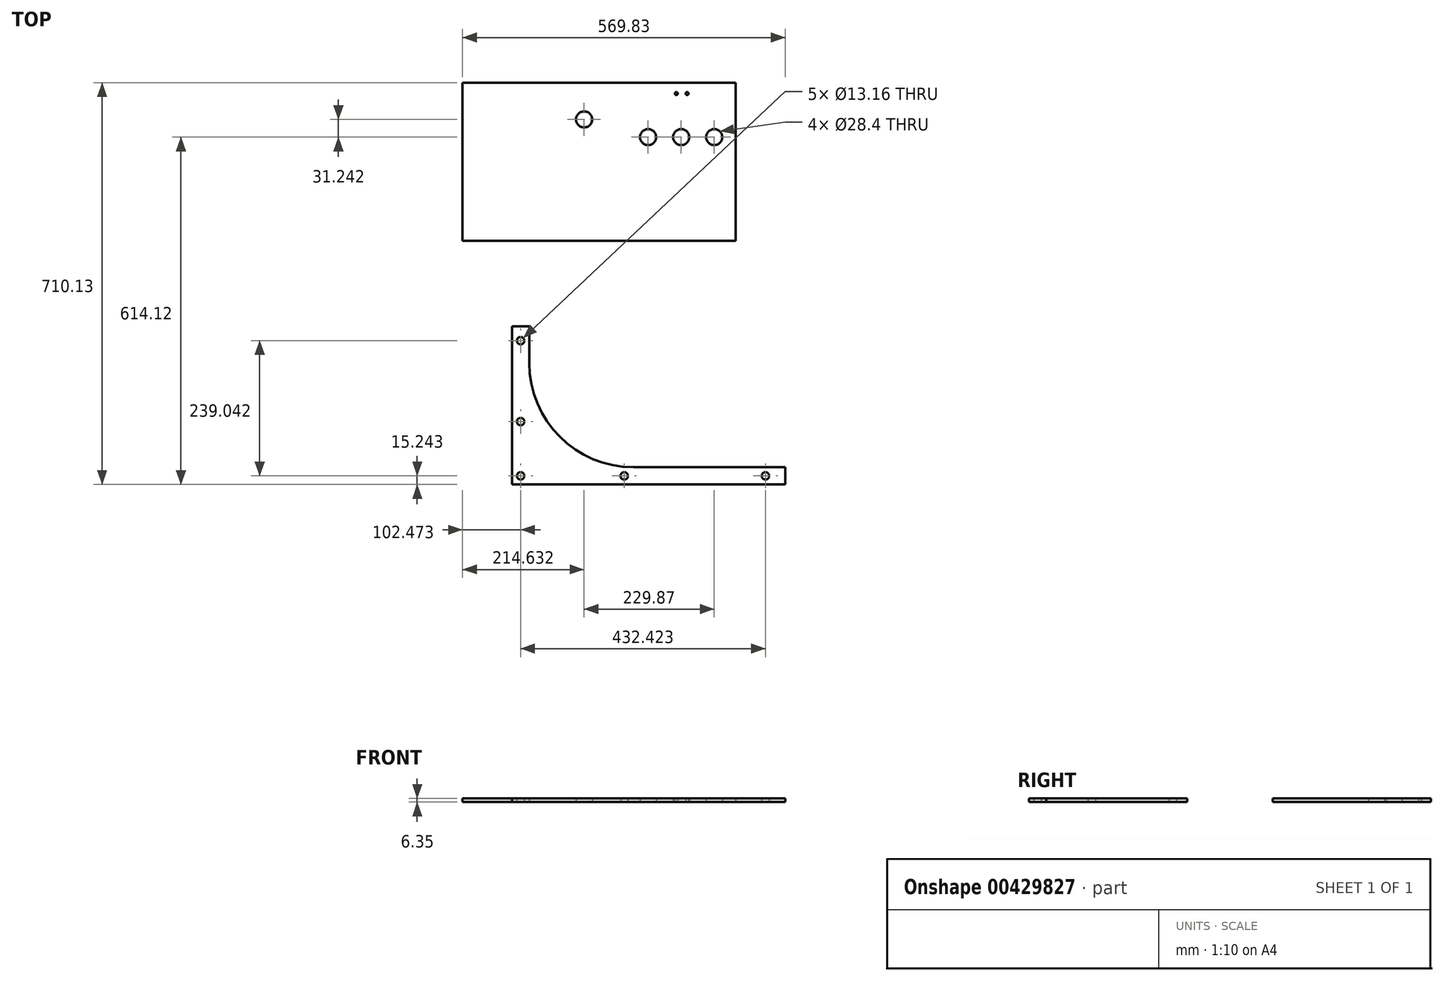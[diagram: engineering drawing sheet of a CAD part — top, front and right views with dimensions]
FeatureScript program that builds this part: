
annotation { "Feature Type Name" : "Feature", "Feature Type Description" : "" }
export const myFeature = defineFeature(function(context is Context, id is Id, definition is map)
    precondition{}
    {
        {
            var Q0;
            Q0=qCreatedBy(makeId("Top.planeOp"),FACE);
            var sketch = newSketch(context, id + "F0", { "sketchPlane" : qUnion([Q0])});
            skLineSegment(sketch, "E0.bottom", {"start": v(-323, 200.73) * mm, "end": v(159.6, 200.73) * mm});
            skLineSegment(sketch, "E0.top", {"start": v(-323, -78.67) * mm, "end": v(159.6, -78.67) * mm});
            skLineSegment(sketch, "E0.left", {"start": v(-323, 200.73) * mm, "end": v(-323, -78.67) * mm});
            skLineSegment(sketch, "E0.right", {"start": v(159.6, 200.73) * mm, "end": v(159.6, -78.67) * mm});
            skPoint(sketch, "E0.middle", {"position": v(-81.7, 61.03) * mm});
            skCircle(sketch, "E1", {"center": v(4.65, 104.72) * mm, "radius": 14.2 * mm});
            skCircle(sketch, "E2", {"center": v(63.07, 104.72) * mm, "radius": 14.2 * mm});
            skCircle(sketch, "E3", {"center": v(121.5, 104.72) * mm, "radius": 14.2 * mm});
            skCircle(sketch, "E4", {"center": v(121.5, 104.72) * mm, "radius": 25.4 * mm, "construction": true});
            skCircle(sketch, "E5", {"center": v(63.07, 104.72) * mm, "radius": 25.4 * mm, "construction": true});
            skCircle(sketch, "E6", {"center": v(4.65, 104.72) * mm, "radius": 25.4 * mm, "construction": true});
            skLineSegment(sketch, "E7", {"start": v(4.65, 104.72) * mm, "end": v(121.5, 104.72) * mm, "construction": true});
            skCircle(sketch, "E8", {"center": v(-108.38, 135.96) * mm, "radius": 50.8 * mm, "construction": true});
            skCircle(sketch, "E9", {"center": v(-108.38, 135.96) * mm, "radius": 14.2 * mm});
            skLineSegment(sketch, "E10", {"start": v(-292.53, 200.73) * mm, "end": v(-292.53, -48.19) * mm, "construction": true});
            skLineSegment(sketch, "E11", {"start": v(-292.53, -48.19) * mm, "end": v(159.6, -48.19) * mm, "construction": true});
            skLineSegment(sketch, "E12", {"start": v(-323, 186.52) * mm, "end": v(-292.53, 186.52) * mm, "construction": true});
            skLineSegment(sketch, "E13", {"start": v(0.65, -78.67) * mm, "end": v(0.65, -48.19) * mm, "construction": true});
            skArc(sketch, "E14", {"start": v(-292.53, 135.96) * mm, "mid": v(-238.6, 5.75) * mm, "end": v(-108.38, -48.19) * mm});
            skCircle(sketch, "E15", {"center": v(404.21, -334.4) * mm, "radius": 63.5 * mm, "construction": true});
            skLineSegment(sketch, "E16.bottom", {"start": v(-235.78, -230) * mm, "end": v(246.82, -230) * mm, "construction": true});
            skLineSegment(sketch, "E16.top", {"start": v(-235.78, -509.4) * mm, "end": v(246.82, -509.4) * mm});
            skLineSegment(sketch, "E16.left", {"start": v(-235.78, -230) * mm, "end": v(-235.78, -509.4) * mm});
            skLineSegment(sketch, "E16.right", {"start": v(246.82, -230) * mm, "end": v(246.82, -509.4) * mm, "construction": true});
            skPoint(sketch, "E16.middle", {"position": v(5.52, -369.7) * mm});
            skCircle(sketch, "E17", {"center": v(91.88, -326) * mm, "radius": 14.2 * mm, "construction": true});
            skCircle(sketch, "E18", {"center": v(150.3, -326) * mm, "radius": 14.2 * mm, "construction": true});
            skCircle(sketch, "E19", {"center": v(208.72, -326) * mm, "radius": 14.2 * mm, "construction": true});
            skCircle(sketch, "E20", {"center": v(208.72, -326) * mm, "radius": 25.4 * mm, "construction": true});
            skCircle(sketch, "E21", {"center": v(150.3, -326) * mm, "radius": 25.4 * mm, "construction": true});
            skCircle(sketch, "E22", {"center": v(91.88, -326) * mm, "radius": 25.4 * mm, "construction": true});
            skLineSegment(sketch, "E23", {"start": v(91.88, -326) * mm, "end": v(208.72, -326) * mm, "construction": true});
            skCircle(sketch, "E24", {"center": v(-21.15, -294.77) * mm, "radius": 50.8 * mm, "construction": true});
            skCircle(sketch, "E25", {"center": v(-21.15, -294.77) * mm, "radius": 14.2 * mm, "construction": true});
            skLineSegment(sketch, "E26", {"start": v(-205.3, -230) * mm, "end": v(-205.3, -294.77) * mm});
            skLineSegment(sketch, "E27", {"start": v(-21.15, -478.92) * mm, "end": v(246.82, -478.92) * mm});
            skLineSegment(sketch, "E28", {"start": v(-235.78, -244.21) * mm, "end": v(-205.3, -244.21) * mm, "construction": true});
            skLineSegment(sketch, "E29", {"start": v(87.88, -509.4) * mm, "end": v(87.88, -478.92) * mm, "construction": true});
            skArc(sketch, "E30", {"start": v(-205.3, -294.77) * mm, "mid": v(-151.36, -424.98) * mm, "end": v(-21.15, -478.92) * mm});
            skCircle(sketch, "E31", {"center": v(211.89, -494.16) * mm, "radius": 6.58 * mm});
            skPoint(sketch, "E31.centerSnap0", {"position": v(87.88, -494.16) * mm});
            skCircle(sketch, "E32", {"center": v(-37.52, -494.16) * mm, "radius": 6.58 * mm});
            skCircle(sketch, "E33", {"center": v(-220.54, -494.16) * mm, "radius": 6.58 * mm});
            skPoint(sketch, "E33.centerSnap0", {"position": v(-220.54, -244.21) * mm});
            skCircle(sketch, "E34", {"center": v(-220.54, -398.2) * mm, "radius": 6.58 * mm});
            skCircle(sketch, "E35", {"center": v(-220.54, -255.12) * mm, "radius": 6.58 * mm});
            skLineSegment(sketch, "E36", {"start": v(-235.78, -230) * mm, "end": v(-205.3, -230) * mm});
            skLineSegment(sketch, "E37", {"start": v(246.82, -478.92) * mm, "end": v(246.82, -509.4) * mm});
            skCircle(sketch, "E38", {"center": v(54.53, 181.56) * mm, "radius": 2.54 * mm});
            skCircle(sketch, "E39", {"center": v(73.58, 181.56) * mm, "radius": 2.54 * mm});
            skSolve(sketch);
        }
        {
            var Q0;
            Q0=makeQuery(id+"F0.imprint","IMPRINT",FACE,{"disambiguationData":[TD([[makeQuery(id+"F0.imprint","IMPRINT",EDGE,{"derivedFrom":sQuery(id+"F0.wireOp",EDGE,"E16.top")}),1.0]])]});
            extrude(context, id + "F1", {"entities" : qUnion([Q0]), "depth" : 6.35 * mm});
        }
        {
            var Q0;
            Q0=makeQuery(id+"F0.imprint","IMPRINT",FACE,{"disambiguationData":[TD([[makeQuery(id+"F0.imprint","IMPRINT",EDGE,{"derivedFrom":sQuery(id+"F0.wireOp",EDGE,"E0.bottom")}),-1.0]])]});
            extrude(context, id + "F2", {"entities" : qUnion([Q0]), "depth" : 6.35 * mm});
        }
    });
